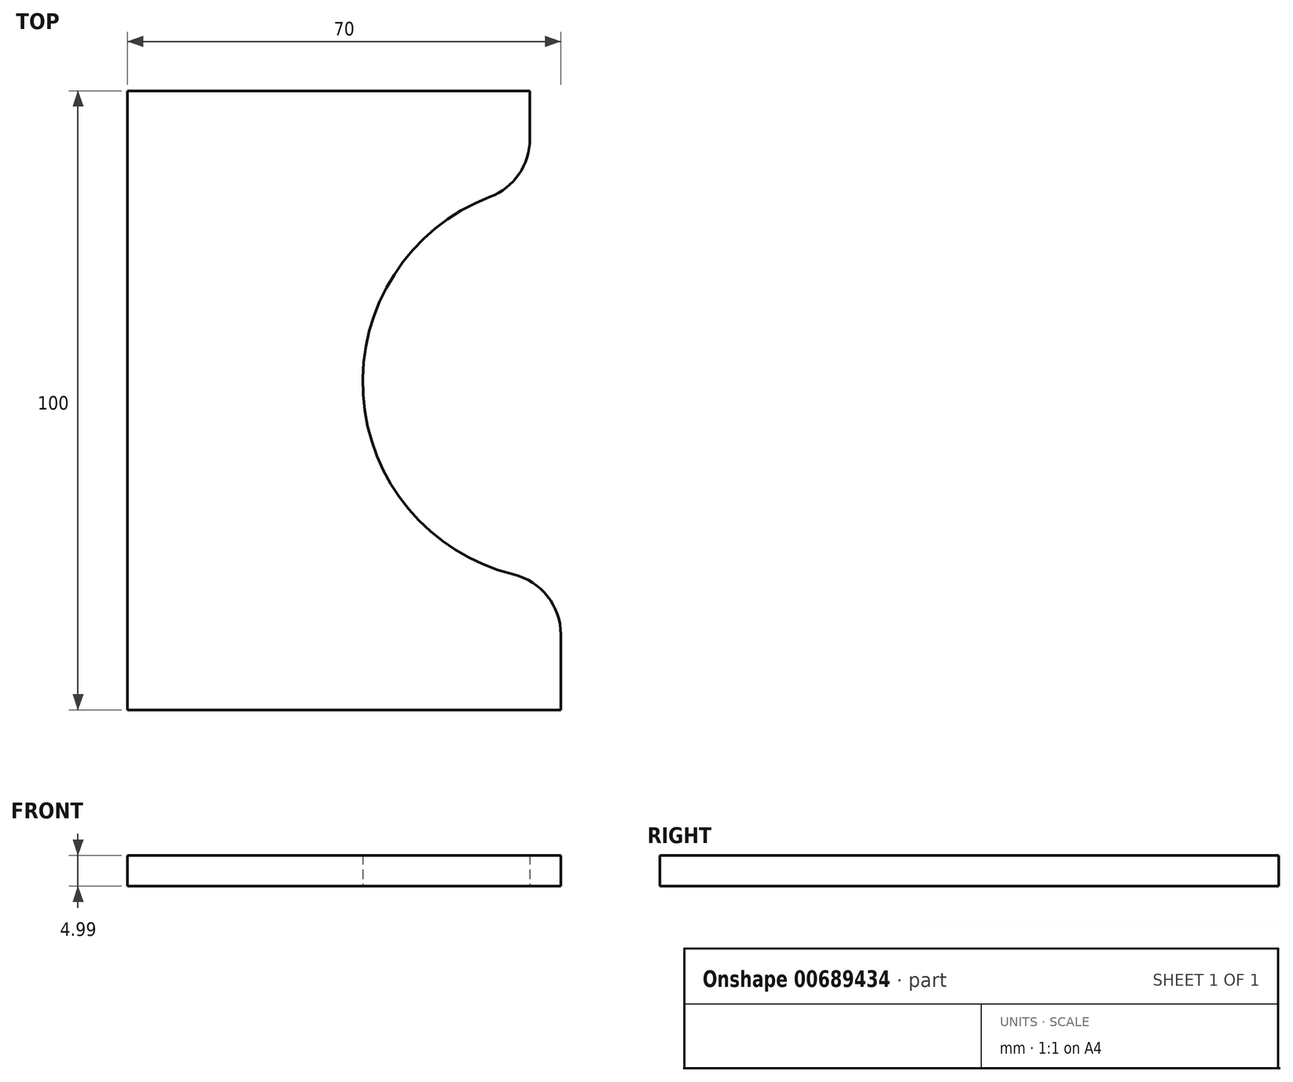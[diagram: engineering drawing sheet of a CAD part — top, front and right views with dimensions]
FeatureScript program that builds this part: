
annotation { "Feature Type Name" : "Feature", "Feature Type Description" : "" }
export const myFeature = defineFeature(function(context is Context, id is Id, definition is map)
    precondition{}
    {
        {
            var Q0;
            Q0=qCreatedBy(makeId("Top.planeOp"),FACE);
            var sketch = newSketch(context, id + "F0", { "sketchPlane" : qUnion([Q0])});
            skLineSegment(sketch, "E0.bottom", {"start": v(-28.6, 47.02) * mm, "end": v(36.4, 47.02) * mm});
            skLineSegment(sketch, "E0.top", {"start": v(-28.6, -52.98) * mm, "end": v(41.4, -52.98) * mm});
            skLineSegment(sketch, "E0.left", {"start": v(-28.6, 47.02) * mm, "end": v(-28.6, -52.98) * mm});
            skArc(sketch, "E1", {"start": v(29.97, 29.91) * mm, "mid": v(9.44, -2) * mm, "end": v(33.78, -31.1) * mm});
            skLineSegment(sketch, "E2", {"start": v(36.4, 47.02) * mm, "end": v(36.4, 39.25) * mm});
            skLineSegment(sketch, "E3.trimOffspring", {"start": v(41.4, -40.81) * mm, "end": v(41.4, -52.98) * mm});
            skPoint(sketch, "E4.orphan", {"position": v(41.4, 47.02) * mm});
            skPoint(sketch, "E5.visualSharp", {"position": v(36.4, 31.63) * mm});
            skArc(sketch, "E5.filletArc", {"start": v(29.97, 29.91) * mm, "mid": v(34.64, 33.58) * mm, "end": v(36.4, 39.25) * mm});
            skPoint(sketch, "E6.visualSharp", {"position": v(41.4, -32.02) * mm});
            skArc(sketch, "E6.filletArc", {"start": v(41.4, -40.81) * mm, "mid": v(39.27, -34.64) * mm, "end": v(33.78, -31.1) * mm});
            skSolve(sketch);
        }
        {
            var Q0;
            Q0=makeQuery(id+"F0.imprint","IMPRINT",FACE,{"disambiguationData":[TD([[makeQuery(id+"F0.imprint","IMPRINT",EDGE,{"derivedFrom":sQuery(id+"F0.wireOp",EDGE,"E0.bottom")}),-1.0]])]});
            extrude(context, id + "F1", {"entities" : qUnion([Q0]), "depth" : 5 * mm, "offsetDistance" : 25 * mm});
        }
    });
